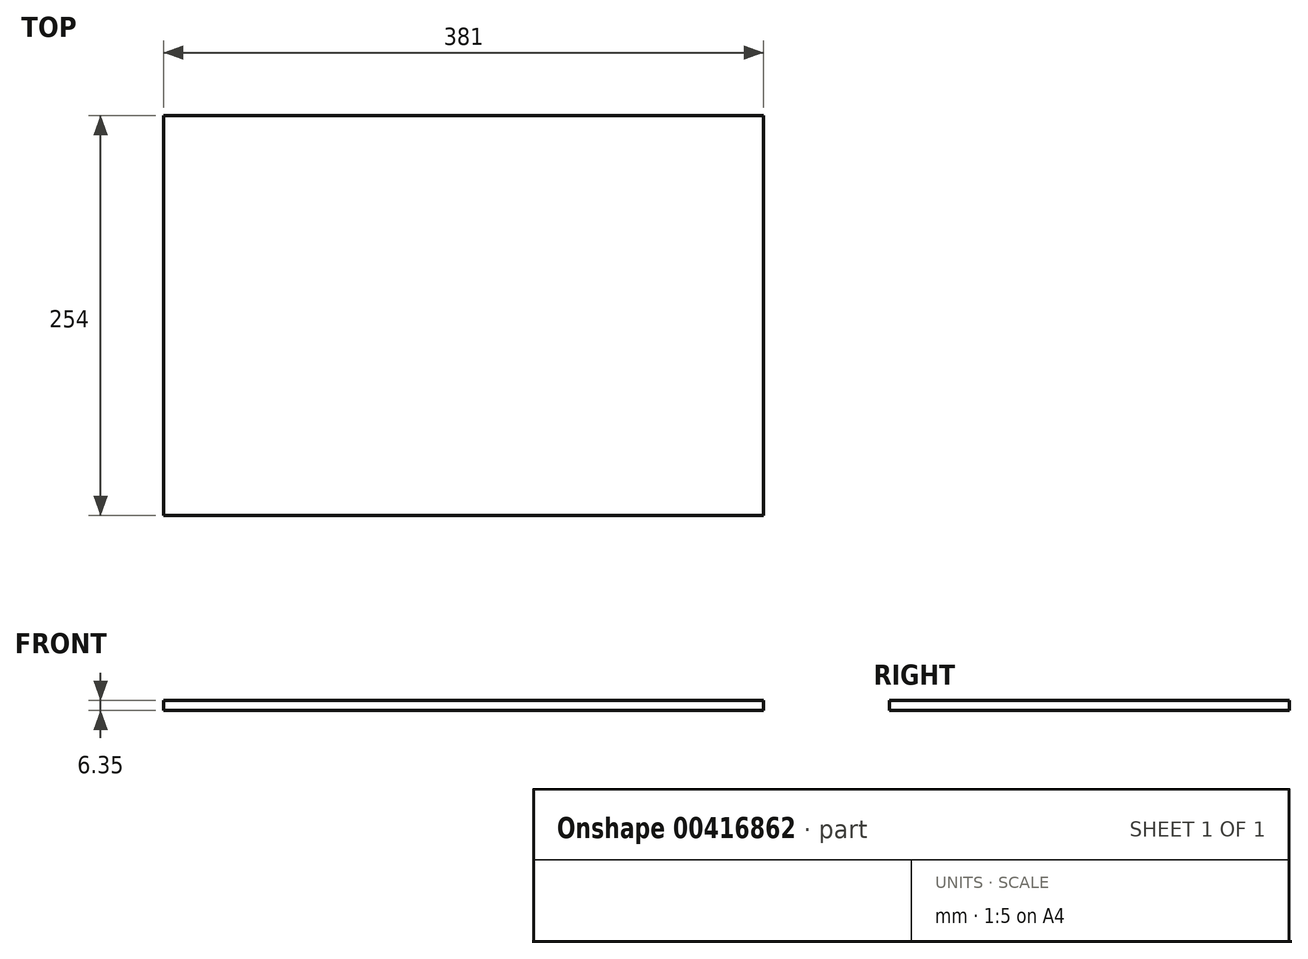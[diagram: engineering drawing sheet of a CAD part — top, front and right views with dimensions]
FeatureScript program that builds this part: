
annotation { "Feature Type Name" : "Feature", "Feature Type Description" : "" }
export const myFeature = defineFeature(function(context is Context, id is Id, definition is map)
    precondition{}
    {
        {
            var Q0;
            Q0=qCreatedBy(makeId("Top.planeOp"),FACE);
            var sketch = newSketch(context, id + "F0", { "sketchPlane" : qUnion([Q0])});
            skLineSegment(sketch, "E0.bottom", {"start": v(-190.5, 127) * mm, "end": v(190.5, 127) * mm});
            skLineSegment(sketch, "E0.top", {"start": v(-190.5, -127) * mm, "end": v(190.5, -127) * mm});
            skLineSegment(sketch, "E0.left", {"start": v(-190.5, 127) * mm, "end": v(-190.5, -127) * mm});
            skLineSegment(sketch, "E0.right", {"start": v(190.5, 127) * mm, "end": v(190.5, -127) * mm});
            skPoint(sketch, "E0.middle", {"position": v(0, 0) * mm});
            skSolve(sketch);
        }
        {
            var Q0;
            Q0 = qSketchRegion(id + "F0", true);
            extrude(context, id + "F1", {"entities" : qUnion([Q0]), "depth" : 6.35 * mm});
        }
    });
